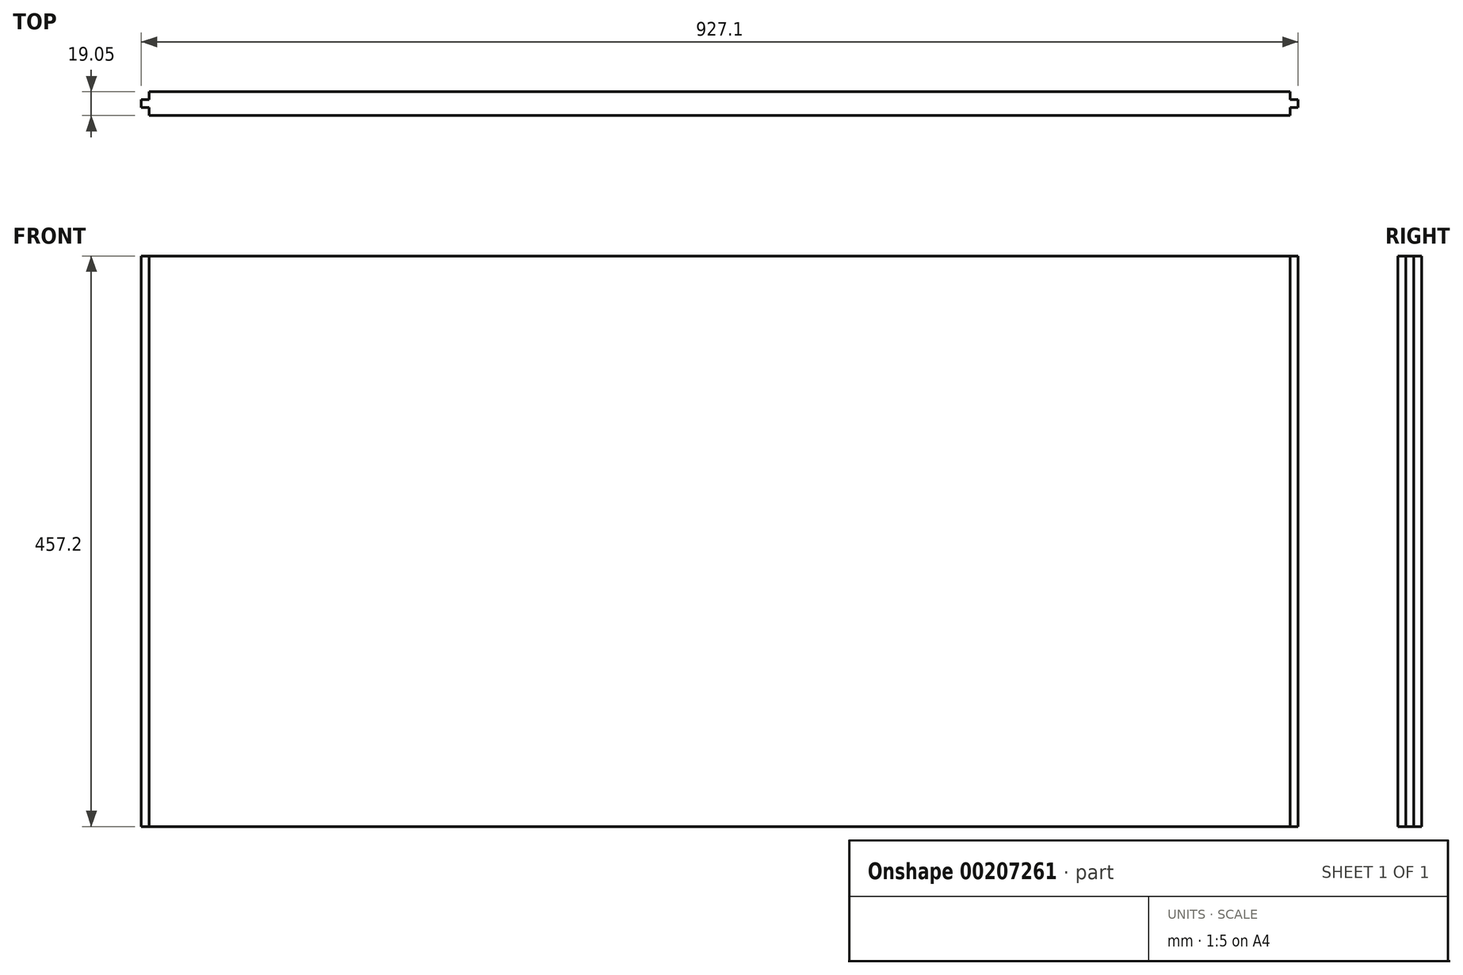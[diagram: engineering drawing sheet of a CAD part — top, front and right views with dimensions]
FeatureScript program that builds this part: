
annotation { "Feature Type Name" : "Feature", "Feature Type Description" : "" }
export const myFeature = defineFeature(function(context is Context, id is Id, definition is map)
    precondition{}
    {
        {
            var Q0;
            Q0=qCreatedBy(makeId("Top.planeOp"),FACE);
            var sketch = newSketch(context, id + "F0", { "sketchPlane" : qUnion([Q0])});
            skLineSegment(sketch, "E0", {"start": v(0, 0) * mm, "end": v(-6.35, 0) * mm});
            skLineSegment(sketch, "E1", {"start": v(-6.35, 0) * mm, "end": v(-6.35, -6.35) * mm});
            skLineSegment(sketch, "E2", {"start": v(-6.35, -6.35) * mm, "end": v(0, -6.35) * mm});
            skLineSegment(sketch, "E3", {"start": v(0, -6.35) * mm, "end": v(0, -12.7) * mm});
            skLineSegment(sketch, "E4", {"start": v(0, -12.7) * mm, "end": v(914.4, -12.7) * mm});
            skLineSegment(sketch, "E5", {"start": v(914.4, -12.7) * mm, "end": v(914.4, -6.35) * mm});
            skLineSegment(sketch, "E6", {"start": v(914.4, -6.35) * mm, "end": v(920.75, -6.35) * mm});
            skLineSegment(sketch, "E7", {"start": v(920.75, -6.35) * mm, "end": v(920.75, 0) * mm});
            skLineSegment(sketch, "E8", {"start": v(920.75, 0) * mm, "end": v(914.4, 0) * mm});
            skLineSegment(sketch, "E9", {"start": v(914.4, 0) * mm, "end": v(914.4, 6.35) * mm});
            skLineSegment(sketch, "E10", {"start": v(914.4, 6.35) * mm, "end": v(0, 6.35) * mm});
            skLineSegment(sketch, "E11", {"start": v(0, 6.35) * mm, "end": v(0, 0) * mm});
            skSolve(sketch);
        }
        {
            var Q0;
            Q0=makeQuery(id+"F0.imprint","IMPRINT",FACE,{"disambiguationData":[TD([[makeQuery(id+"F0.imprint","IMPRINT",EDGE,{"derivedFrom":sQuery(id+"F0.wireOp",EDGE,"E0")}),1.0]])]});
            extrude(context, id + "F1", {"entities" : qUnion([Q0]), "depth" : 457.2 * mm});
        }
    });
